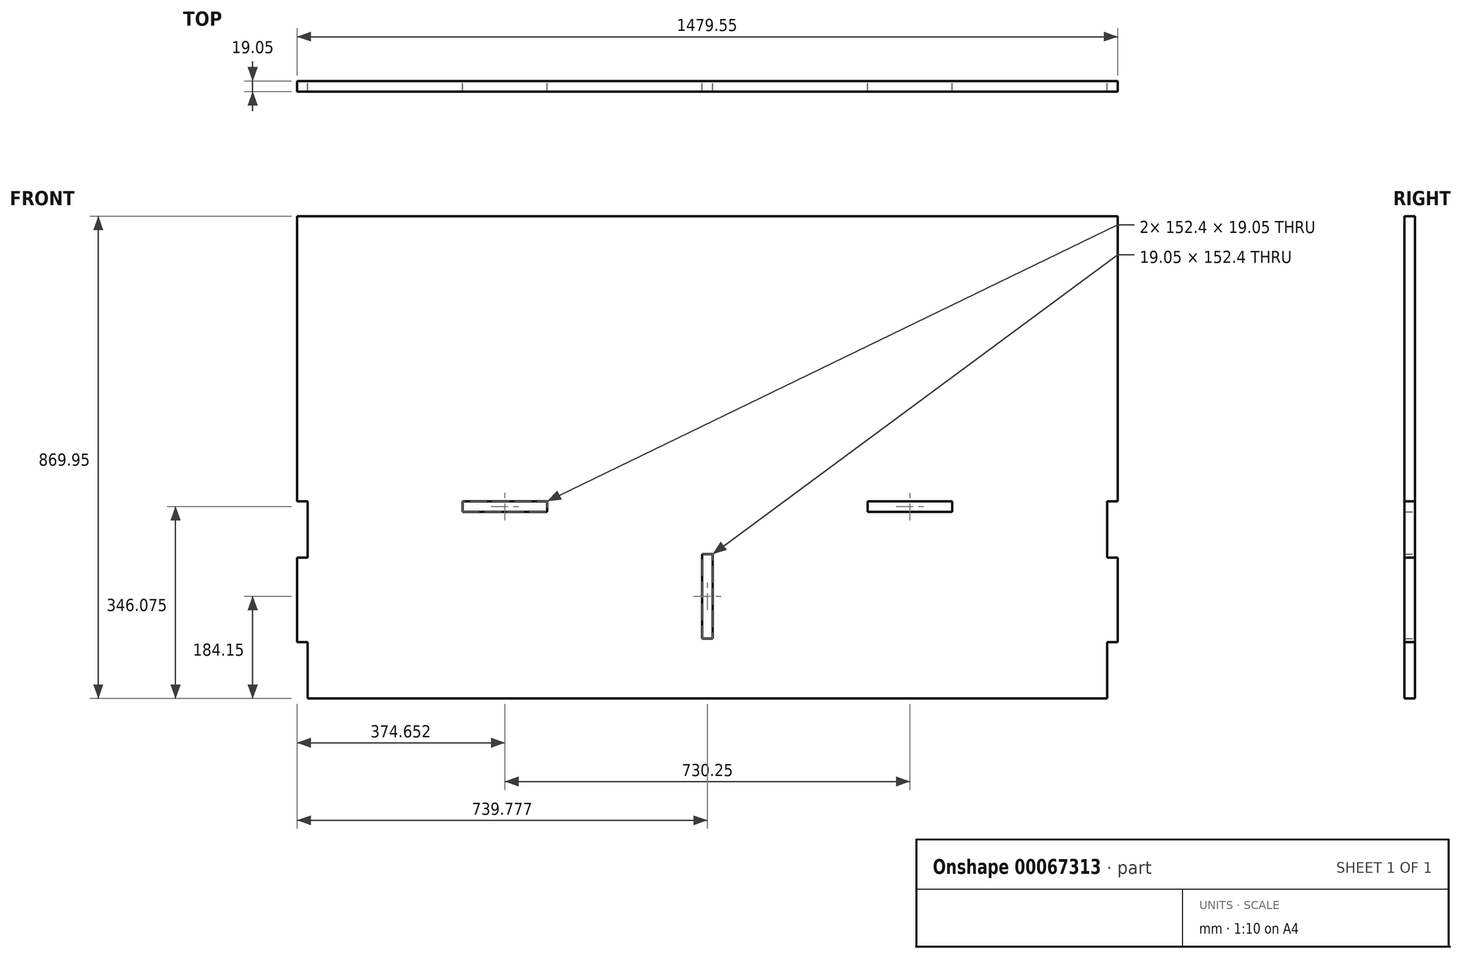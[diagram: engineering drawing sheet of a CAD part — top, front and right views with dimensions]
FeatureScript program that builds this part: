
annotation { "Feature Type Name" : "Feature", "Feature Type Description" : "" }
export const myFeature = defineFeature(function(context is Context, id is Id, definition is map)
    precondition{}
    {
        {
            var Q0;
            Q0=qCreatedBy(makeId("Front.planeOp"),FACE);
            var sketch = newSketch(context, id + "F0", { "sketchPlane" : qUnion([Q0])});
            skLineSegment(sketch, "E0.top", {"start": v(-683.7, -355.6) * mm, "end": v(757.74, -355.6) * mm});
            skLineSegment(sketch, "E0.left", {"start": v(-683.7, 0) * mm, "end": v(-683.7, -355.6) * mm});
            skLineSegment(sketch, "E0.right", {"start": v(757.74, 0) * mm, "end": v(757.74, -355.6) * mm});
            skLineSegment(sketch, "E1.bottom", {"start": v(-404.3, -355.6) * mm, "end": v(-251.9, -355.6) * mm});
            skLineSegment(sketch, "E2.bottom", {"start": v(325.94, -355.6) * mm, "end": v(478.34, -355.6) * mm});
            skLineSegment(sketch, "E3.bottom", {"start": v(27.5, -95.25) * mm, "end": v(46.54, -95.25) * mm});
            skLineSegment(sketch, "E3.top", {"start": v(27.5, -247.65) * mm, "end": v(46.54, -247.65) * mm});
            skLineSegment(sketch, "E3.left", {"start": v(27.5, -95.25) * mm, "end": v(27.5, -247.65) * mm});
            skLineSegment(sketch, "E3.right", {"start": v(46.54, -95.25) * mm, "end": v(46.54, -247.65) * mm});
            skLineSegment(sketch, "E4.bottom", {"start": v(-404.3, 0) * mm, "end": v(-251.9, 0) * mm});
            skLineSegment(sketch, "E4.top", {"start": v(-404.3, -19.05) * mm, "end": v(-251.9, -19.05) * mm});
            skLineSegment(sketch, "E4.left", {"start": v(-404.3, 0) * mm, "end": v(-404.3, -19.05) * mm});
            skLineSegment(sketch, "E4.right", {"start": v(-251.9, 0) * mm, "end": v(-251.9, -19.05) * mm});
            skLineSegment(sketch, "E5.bottom", {"start": v(325.94, 0) * mm, "end": v(478.34, 0) * mm});
            skLineSegment(sketch, "E5.top", {"start": v(325.94, -19.05) * mm, "end": v(478.34, -19.05) * mm});
            skLineSegment(sketch, "E5.left", {"start": v(325.94, 0) * mm, "end": v(325.94, -19.05) * mm});
            skLineSegment(sketch, "E5.right", {"start": v(478.34, 0) * mm, "end": v(478.34, -19.05) * mm});
            skLineSegment(sketch, "E6.bottom", {"start": v(757.74, -254) * mm, "end": v(776.8, -254) * mm});
            skLineSegment(sketch, "E6.top", {"start": v(757.74, -101.6) * mm, "end": v(776.8, -101.6) * mm});
            skLineSegment(sketch, "E6.left", {"start": v(757.74, -254) * mm, "end": v(757.74, -101.6) * mm});
            skLineSegment(sketch, "E6.right", {"start": v(776.8, -254) * mm, "end": v(776.8, -101.6) * mm});
            skLineSegment(sketch, "E7.bottom", {"start": v(-683.7, -254) * mm, "end": v(-702.76, -254) * mm});
            skLineSegment(sketch, "E7.top", {"start": v(-683.7, -101.6) * mm, "end": v(-702.76, -101.6) * mm});
            skLineSegment(sketch, "E7.left", {"start": v(-683.7, -254) * mm, "end": v(-683.7, -101.6) * mm});
            skLineSegment(sketch, "E7.right", {"start": v(-702.76, -254) * mm, "end": v(-702.76, -101.6) * mm});
            skLineSegment(sketch, "E8.top", {"start": v(-404.3, -374.65) * mm, "end": v(-251.9, -374.65) * mm});
            skLineSegment(sketch, "E8.left", {"start": v(-404.3, -355.6) * mm, "end": v(-404.3, -374.65) * mm});
            skLineSegment(sketch, "E8.right", {"start": v(-251.9, -355.6) * mm, "end": v(-251.9, -374.65) * mm});
            skLineSegment(sketch, "E9.top", {"start": v(325.94, -374.65) * mm, "end": v(478.34, -374.65) * mm});
            skLineSegment(sketch, "E9.left", {"start": v(325.94, -355.6) * mm, "end": v(325.94, -374.65) * mm});
            skLineSegment(sketch, "E9.right", {"start": v(478.34, -355.6) * mm, "end": v(478.34, -374.65) * mm});
            skLineSegment(sketch, "E10", {"start": v(-683.7, 0) * mm, "end": v(-702.76, 0) * mm});
            skLineSegment(sketch, "E11", {"start": v(757.74, -101.6) * mm, "end": v(757.74, 0) * mm});
            skLineSegment(sketch, "E12", {"start": v(757.74, 0) * mm, "end": v(776.8, 0) * mm});
            skLineSegment(sketch, "E13", {"start": v(-702.76, 514.35) * mm, "end": v(776.8, 514.35) * mm});
            skLineSegment(sketch, "E14", {"start": v(776.8, 0) * mm, "end": v(776.8, 514.35) * mm});
            skLineSegment(sketch, "E15", {"start": v(-702.76, 0) * mm, "end": v(-702.76, 514.35) * mm});
            skLineSegment(sketch, "E16.bottom", {"start": v(-474.16, 514.35) * mm, "end": v(-321.76, 514.35) * mm});
            skLineSegment(sketch, "E16.top", {"start": v(-474.16, 533.4) * mm, "end": v(-321.76, 533.4) * mm});
            skLineSegment(sketch, "E16.left", {"start": v(-474.16, 514.35) * mm, "end": v(-474.16, 533.4) * mm});
            skLineSegment(sketch, "E16.right", {"start": v(-321.76, 514.35) * mm, "end": v(-321.76, 533.4) * mm});
            skLineSegment(sketch, "E17.bottom", {"start": v(395.8, 514.35) * mm, "end": v(548.2, 514.35) * mm});
            skLineSegment(sketch, "E17.top", {"start": v(395.8, 533.4) * mm, "end": v(548.2, 533.4) * mm});
            skLineSegment(sketch, "E17.left", {"start": v(395.8, 514.35) * mm, "end": v(395.8, 533.4) * mm});
            skLineSegment(sketch, "E17.right", {"start": v(548.2, 514.35) * mm, "end": v(548.2, 533.4) * mm});
            skSolve(sketch);
        }
        {
            var Q0;
            Q0=makeQuery(id+"F0.imprint","IMPRINT",FACE,{"disambiguationData":[TD([[makeQuery(id+"F0.imprint","IMPRINT",EDGE,{"derivedFrom":sQuery(id+"F0.wireOp",EDGE,"E7.bottom")}),-1.0]])]});
            var Q1;
            Q1=makeQuery(id+"F0.imprint","IMPRINT",FACE,{"disambiguationData":[TD([[makeQuery(id+"F0.imprint","IMPRINT",EDGE,{"derivedFrom":sQuery(id+"F0.wireOp",EDGE,"E6.bottom")}),1.0]])]});
            var Q2;
            Q2=makeQuery(id+"F0.imprint","IMPRINT",FACE,{"disambiguationData":[TD([[makeQuery(id+"F0.imprint","IMPRINT",EDGE,{"derivedFrom":sQuery(id+"F0.wireOp",EDGE,"E1.bottom")}),-1.0]])]});
            var Q3;
            Q3=makeQuery(id+"F0.imprint","IMPRINT",FACE,{"disambiguationData":[TD([[makeQuery(id+"F0.imprint","IMPRINT",EDGE,{"derivedFrom":sQuery(id+"F0.wireOp",EDGE,"E2.bottom")}),-1.0]])]});
            var Q4;
            {var subQ5=sQuery(id+"F0.wireOp",EDGE,"E0.right");Q4=makeQuery(id+"F0.imprint","IMPRINT",FACE,{"disambiguationData":[TD([[makeQuery(id+"F0.imprint","IMPRINT",EDGE,{"derivedFrom":subQ5}),-1.0]])]});}
            var Q5;
            Q5=makeQuery(id+"F0.imprint","IMPRINT",FACE,{"disambiguationData":[TD([[makeQuery(id+"F0.imprint","IMPRINT",EDGE,{"derivedFrom":sQuery(id+"F0.wireOp",EDGE,"E16.bottom")}),1.0]])]});
            var Q6;
            Q6=makeQuery(id+"F0.imprint","IMPRINT",FACE,{"disambiguationData":[TD([[makeQuery(id+"F0.imprint","IMPRINT",EDGE,{"derivedFrom":sQuery(id+"F0.wireOp",EDGE,"E17.bottom")}),1.0]])]});
            extrude(context, id + "F1", {"entities" : qUnion([Q0, Q1, Q2, Q3, Q4, Q5, Q6]), "depth" : 19.05 * mm});
        }
    });
